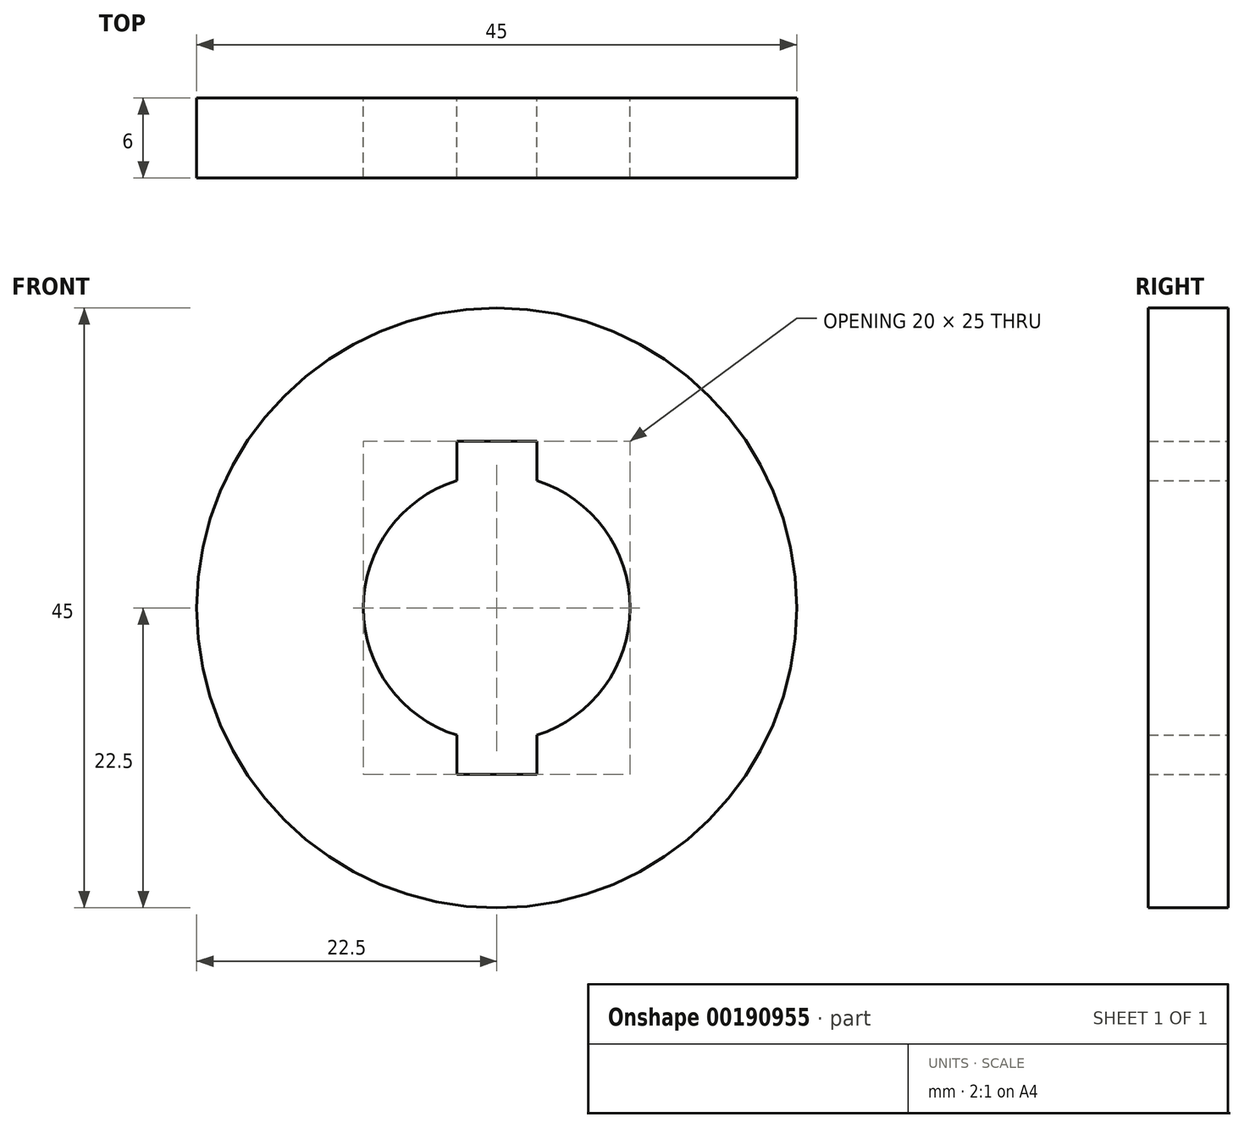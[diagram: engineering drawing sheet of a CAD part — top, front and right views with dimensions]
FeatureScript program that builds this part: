
annotation { "Feature Type Name" : "Feature", "Feature Type Description" : "" }
export const myFeature = defineFeature(function(context is Context, id is Id, definition is map)
    precondition{}
    {
        {
            var Q0;
            Q0=qCreatedBy(makeId("Front.planeOp"),FACE);
            var sketch = newSketch(context, id + "F0", { "sketchPlane" : qUnion([Q0])});
            skCircle(sketch, "E0", {"center": v(0, 0) * mm, "radius": 22.5 * mm});
            skCircle(sketch, "E1", {"center": v(0, 0) * mm, "radius": 10 * mm});
            skLineSegment(sketch, "E2.bottom", {"start": v(-3, 6.5) * mm, "end": v(3, 6.5) * mm});
            skLineSegment(sketch, "E2.top", {"start": v(-3, 12.5) * mm, "end": v(3, 12.5) * mm});
            skLineSegment(sketch, "E2.left", {"start": v(-3, 6.5) * mm, "end": v(-3, 12.5) * mm});
            skLineSegment(sketch, "E2.right", {"start": v(3, 6.5) * mm, "end": v(3, 12.5) * mm});
            skLineSegment(sketch, "E3.bottom", {"start": v(-3, -12.5) * mm, "end": v(3, -12.5) * mm});
            skLineSegment(sketch, "E3.top", {"start": v(-3, -6.5) * mm, "end": v(3, -6.5) * mm});
            skLineSegment(sketch, "E3.left", {"start": v(-3, -12.5) * mm, "end": v(-3, -6.5) * mm});
            skLineSegment(sketch, "E3.right", {"start": v(3, -12.5) * mm, "end": v(3, -6.5) * mm});
            skSolve(sketch);
        }
        {
            var Q0;
            Q0=makeQuery(id+"F0.imprint","IMPRINT",FACE,{"disambiguationData":[TD([[makeQuery(id+"F0.imprint","IMPRINT",EDGE,{"derivedFrom":sQuery(id+"F0.wireOp",EDGE,"E0")}),1.0]])]});
            extrude(context, id + "F1", {"entities" : qUnion([Q0]), "depth" : 6 * mm});
        }
    });
